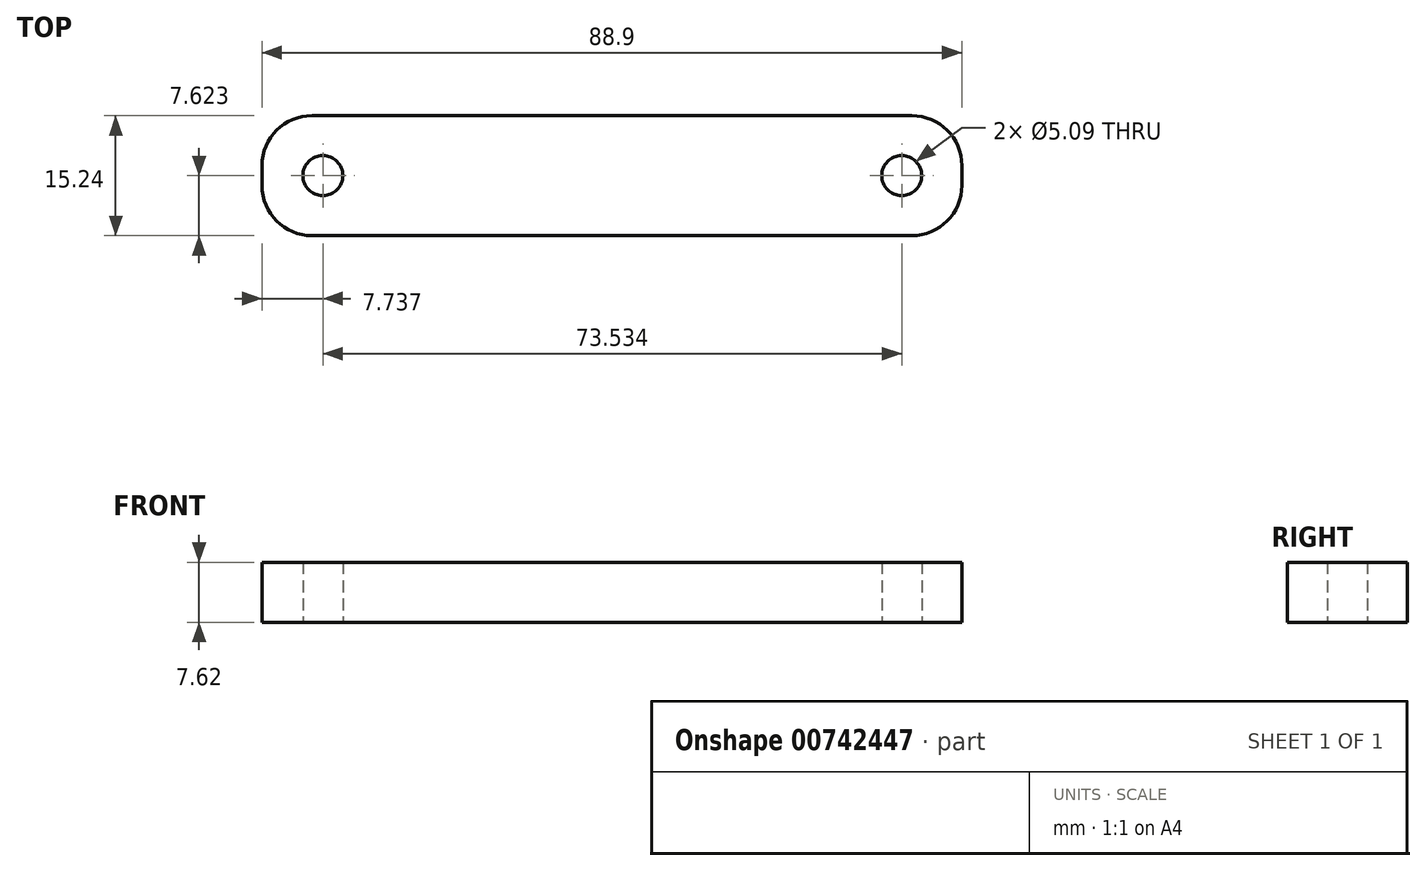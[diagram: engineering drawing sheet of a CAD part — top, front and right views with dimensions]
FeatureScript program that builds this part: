
annotation { "Feature Type Name" : "Feature", "Feature Type Description" : "" }
export const myFeature = defineFeature(function(context is Context, id is Id, definition is map)
    precondition{}
    {
        {
            var Q0;
            Q0=qCreatedBy(makeId("Top.planeOp"),FACE);
            var sketch = newSketch(context, id + "F0", { "sketchPlane" : qUnion([Q0])});
            skLineSegment(sketch, "E0.bottom", {"start": v(-31.91, 3.41) * mm, "end": v(44.29, 3.41) * mm});
            skLineSegment(sketch, "E0.top", {"start": v(-31.91, -11.83) * mm, "end": v(44.29, -11.83) * mm});
            skLineSegment(sketch, "E0.left", {"start": v(-38.26, -2.94) * mm, "end": v(-38.26, -5.48) * mm});
            skLineSegment(sketch, "E0.right", {"start": v(50.64, -2.94) * mm, "end": v(50.64, -5.48) * mm});
            skCircle(sketch, "E1", {"center": v(-30.52, -4.2) * mm, "radius": 2.54 * mm});
            skCircle(sketch, "E2", {"center": v(43.01, -4.2) * mm, "radius": 2.54 * mm});
            skPoint(sketch, "E3.visualSharp", {"position": v(-38.26, 3.41) * mm});
            skArc(sketch, "E3.filletArc", {"start": v(-31.91, 3.41) * mm, "mid": v(-36.4, 1.55) * mm, "end": v(-38.26, -2.94) * mm});
            skPoint(sketch, "E4.visualSharp", {"position": v(-38.26, -11.83) * mm});
            skArc(sketch, "E4.filletArc", {"start": v(-38.26, -5.48) * mm, "mid": v(-36.4, -9.97) * mm, "end": v(-31.91, -11.83) * mm});
            skPoint(sketch, "E5.visualSharp", {"position": v(50.64, 3.41) * mm});
            skArc(sketch, "E5.filletArc", {"start": v(50.64, -2.94) * mm, "mid": v(48.78, 1.55) * mm, "end": v(44.29, 3.41) * mm});
            skPoint(sketch, "E6.visualSharp", {"position": v(50.64, -11.83) * mm});
            skArc(sketch, "E6.filletArc", {"start": v(44.29, -11.83) * mm, "mid": v(48.78, -9.97) * mm, "end": v(50.64, -5.48) * mm});
            skSolve(sketch);
        }
        {
            var Q0;
            Q0 = qSketchRegion(id + "F0", true);
            extrude(context, id + "F1", {"entities" : qUnion([Q0]), "depth" : 7.62 * mm, "offsetDistance" : 25.4 * mm});
        }
    });
